# Revit family: Platek_Menhir_2_Openings
name_source: partatom
category: Apparecchi per illuminazione
revit_build: Autodesk Revit 2017 (Build: 20160225_1515(x64)
units: mm (PartAtom-declared; Revit-internal decimal feet)

## family parameters
Basato su piano di lavoro = Sì
Condiviso = Sì
Punto di calcolo locali = No
Quota connettore circolare = Usa diametro
Sempre verticale = No
Sorgente d'illuminazione = No
Taglio con vuoti quando caricato = No
Tipo di parte = Normale

## types (3) — shared parameters
Aluminium = PLK_Aluminium
Body = PLK_Grey
CRI = >80
Carico apparente = 0 VA
Colour Temperature = 3000 K
Commenti sul tipo = Pedestrian areas, Urban zones, Paths, Roads
Descrizione = Outdoor Lighting, Floor/Ground Illumination
Diffuse Type = PMMA
Dimmable = No
Energy Efficiency Rating = A/A+/A++
Frequency = 50/60 Hz
IK Rating = IK 08
IP Rating = IP65
LED Protection = Surge protection included
Lampada = LED
Light Source = PLK_Light Source
Modello = MENHIR
Mounting Type = Ground
Nota chiave = Other Led colors available on request
PLATEK FInishes = Painted Aluminium, Avalaible in Grey/White/Bronze/Black/Anthracite
Power Supply Unit = Included
Product Documentation Link = http://www.platek.eu
Product Page URL = http://www.platek.eu
Produttore = PLATEK SRL
Prospetto di default = 1219 mm
Supply Voltage = 230 V
Supply Voltage Max = 240 V
Supply Voltage Min = 220 V
URL = www.platek.eu

## per-type parameters (varying)
| type | Angolo di inclinazione | Cable Lenght | Codice assieme | Height | Height1050 | Height200 | Height620 | Immagine tipo | Insulation Class | Luminaire Luminous Flux | Luminaire Luminous Intensity | Luminaire Wattage | Manufacturer Comment | PLATEK Article Code | PLK_Photometric | Product Dimension |
| 4032612_15,3W_LED_3000K_H200mm | 0.00° | Ø4,5÷10mm | 4032612.06(Grey); 4032612.08(Anthracite); 4032612.01(Black); 4032612.02(White); 4032612.07(Corten); 4032612.09(Bronze) | 210 mm  [stored 0.688976 ft] | No | Sì | No | menhir_led_dim1.jpg | 1 | 917 lm | 350 cd | 15 W | 5mmThick PMMA | 4032612 | PLK_Photometrics_4032612 | D200mm x H200mm |
| 4082612_40,2W_LED_3000K_H1050mm | 90.00° | 1,5m (3x1mm^2) | 4082612.06(Grey); 4082612.08(Anthracite); 4082612.01(Black);  4082612.01(Black);  4082612.02(White);  4082612.07(Corten);  4082612.09(Bronze) | 1050 mm | Sì | No | No | menhir_led_dim3.jpg | 2 | 2501 lm | 954 cd | 40 W | 4mm Thick PMMA | 4082612 | PLK_Photometrics_4082612 | D200mm x H800mm |
| 4052612_20,3W_LED_3000K_H620mm | 90.00° | 1m (3x1mm^2) | 4052612.06(Grey); 4052612.08(Anthracite); 4052612.01(Black); 4052612.02(White); 4052612.07(Corten); 4052612.09(Bronze) | 620 mm  [stored 2.03412 ft] | No | No | Sì | menhir_led_dim2.jpg | 1 | 1242 lm | 474 cd | 20 W | 4mm Thick PMMA | 4052612 | PLK_Photometrics_4052612 | D200mm x H620mm |

note: [stored X ft] marks values corroborated as IEEE doubles in the binary element streams (Revit-internal decimal feet)
